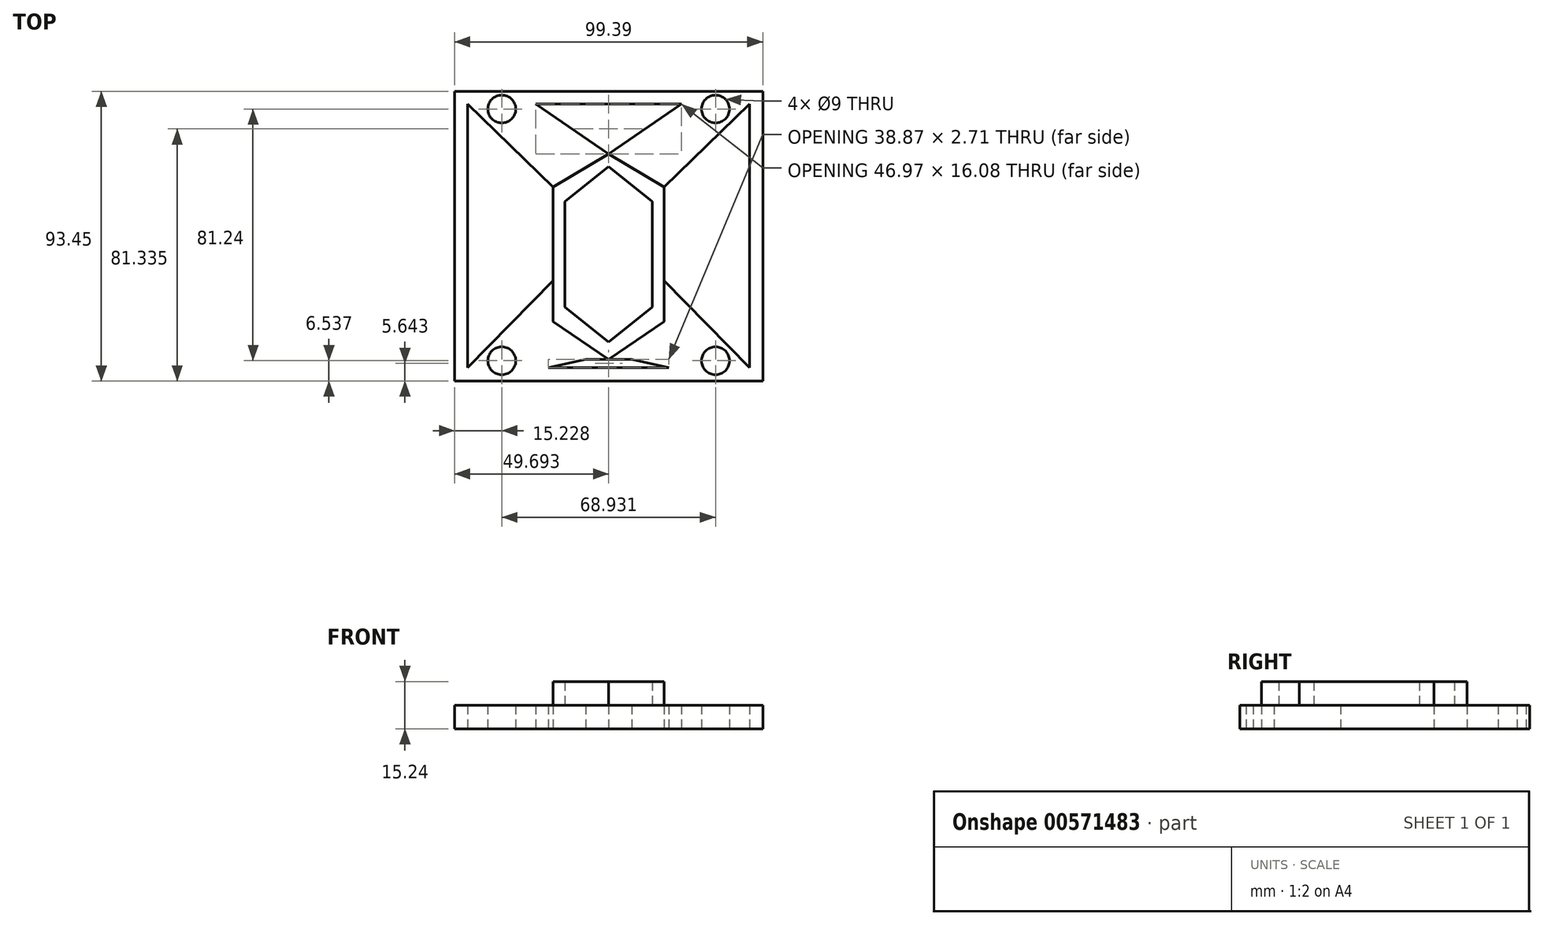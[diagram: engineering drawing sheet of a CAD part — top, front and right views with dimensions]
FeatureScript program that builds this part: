
annotation { "Feature Type Name" : "Feature", "Feature Type Description" : "" }
export const myFeature = defineFeature(function(context is Context, id is Id, definition is map)
    precondition{}
    {
        {
            var Q0;
            Q0=qCreatedBy(makeId("Top.planeOp"),FACE);
            var sketch = newSketch(context, id + "F0", { "sketchPlane" : qUnion([Q0])});
            skLineSegment(sketch, "E0", {"start": v(-15.3, -5.51) * mm, "end": v(-0.48, -5.51) * mm});
            skLineSegment(sketch, "E1", {"start": v(30.61, -12.51) * mm, "end": v(41.8, -12.51) * mm});
            skLineSegment(sketch, "E2.MirrorCS", {"start": v(-46.39, -12.51) * mm, "end": v(-57.58, -12.51) * mm});
            skLineSegment(sketch, "E3", {"start": v(41.8, 80.94) * mm, "end": v(21.56, 80.94) * mm});
            skLineSegment(sketch, "E4.MirrorCS", {"start": v(-57.58, 80.94) * mm, "end": v(-37.33, 80.94) * mm});
            skLineSegment(sketch, "E5", {"start": v(-25.8, 19.92) * mm, "end": v(-25.8, 41.41) * mm});
            skLineSegment(sketch, "E6", {"start": v(10.02, 19.92) * mm, "end": v(10.02, 41.41) * mm});
            skLineSegment(sketch, "E7", {"start": v(-25.8, 41.41) * mm, "end": v(-25.8, 50.1) * mm});
            skLineSegment(sketch, "E8", {"start": v(10.02, 41.41) * mm, "end": v(10.02, 50.1) * mm});
            skLineSegment(sketch, "E9", {"start": v(-37.33, 80.94) * mm, "end": v(21.56, 80.94) * mm});
            skLineSegment(sketch, "E10", {"start": v(15.6, 76.86) * mm, "end": v(-31.37, 76.86) * mm});
            skLineSegment(sketch, "E11", {"start": v(-57.58, 80.94) * mm, "end": v(-57.58, -12.51) * mm});
            skLineSegment(sketch, "E12", {"start": v(-46.39, -12.51) * mm, "end": v(30.61, -12.51) * mm});
            skLineSegment(sketch, "E13", {"start": v(41.8, -12.51) * mm, "end": v(41.8, 80.94) * mm});
            skLineSegment(sketch, "E14", {"start": v(37.6, 76.86) * mm, "end": v(37.6, -8.22) * mm});
            skLineSegment(sketch, "E15", {"start": v(11.55, -8.22) * mm, "end": v(-27.32, -8.22) * mm});
            skLineSegment(sketch, "E16", {"start": v(-53.38, -8.22) * mm, "end": v(-53.38, 76.86) * mm});
            skLineSegment(sketch, "E17", {"start": v(-7.89, 60.79) * mm, "end": v(-7.89, -5.51) * mm, "construction": true});
            skLineSegment(sketch, "E18", {"start": v(-53.38, 76.86) * mm, "end": v(-25.8, 50.1) * mm});
            skLineSegment(sketch, "E19", {"start": v(-31.37, 76.86) * mm, "end": v(-7.89, 60.79) * mm});
            skLineSegment(sketch, "E20", {"start": v(15.6, 76.86) * mm, "end": v(-7.89, 60.79) * mm});
            skLineSegment(sketch, "E21", {"start": v(10.02, 50.1) * mm, "end": v(37.6, 76.86) * mm});
            skLineSegment(sketch, "E22", {"start": v(-25.8, 19.92) * mm, "end": v(-53.38, -8.22) * mm});
            skLineSegment(sketch, "E23", {"start": v(10.02, 19.92) * mm, "end": v(37.6, -8.22) * mm});
            skLineSegment(sketch, "E24", {"start": v(-15.3, -5.51) * mm, "end": v(-27.32, -8.22) * mm});
            skLineSegment(sketch, "E25", {"start": v(-0.48, -5.51) * mm, "end": v(11.55, -8.22) * mm});
            skCircle(sketch, "E26", {"center": v(-42.35, 75.27) * mm, "radius": 4.5 * mm});
            skCircle(sketch, "E27", {"center": v(-42.35, -5.97) * mm, "radius": 4.5 * mm});
            skCircle(sketch, "E28.MirrorC", {"center": v(26.58, 75.27) * mm, "radius": 4.5 * mm});
            skCircle(sketch, "E29.MirrorC", {"center": v(26.58, -5.97) * mm, "radius": 4.5 * mm});
            skSolve(sketch);
        }
        {
            var Q0;
            {var subQ27=sQuery(id+"F0.wireOp",EDGE,"E0");Q0=makeQuery(id+"F0.imprint","IMPRINT",FACE,{"disambiguationData":[TD([[makeQuery(id+"F0.imprint","IMPRINT",EDGE,{"derivedFrom":subQ27}),1.0]])]});}
            var Q1;
            {var subQ0=sQuery(id+"F0.wireOp",EDGE,"E11");Q1=makeQuery(id+"F0.imprint","IMPRINT",FACE,{"disambiguationData":[TD([[makeQuery(id+"F0.imprint","IMPRINT",EDGE,{"derivedFrom":subQ0}),1.0]])]});}
            var Q2;
            {var subQ0=sQuery(id+"F0.wireOp",EDGE,"E13");Q2=makeQuery(id+"F0.imprint","IMPRINT",FACE,{"disambiguationData":[TD([[makeQuery(id+"F0.imprint","IMPRINT",EDGE,{"derivedFrom":subQ0}),1.0]])]});}
            var Q3;
            {var subQ0=sQuery(id+"F0.wireOp",EDGE,"E12");Q3=makeQuery(id+"F0.imprint","IMPRINT",FACE,{"disambiguationData":[TD([[makeQuery(id+"F0.imprint","IMPRINT",EDGE,{"derivedFrom":subQ0}),1.0]])]});}
            var Q4;
            {var subQ0=sQuery(id+"F0.wireOp",EDGE,"E9");Q4=makeQuery(id+"F0.imprint","IMPRINT",FACE,{"disambiguationData":[TD([[makeQuery(id+"F0.imprint","IMPRINT",EDGE,{"derivedFrom":subQ0}),-1.0]])]});}
            extrude(context, id + "F1", {"entities" : qUnion([Q0, Q1, Q2, Q3, Q4]), "depth" : 7.62 * mm, "offsetDistance" : 25.4 * mm});
        }
        {
            var Q0;
            Q0=makeQuery(id+"F1.opExtrude","CAP_FACE",FACE,{"disambiguationData":[OSD([sQuery(id+"F0.wireOp",EDGE,"E0"),sQuery(id+"F0.wireOp",EDGE,"E1"),sQuery(id+"F0.wireOp",EDGE,"E2.MirrorCS"),sQuery(id+"F0.wireOp",EDGE,"WnM6ga3W-2w0Y-njnw-gc1i-JW5yFLPxI45b"),sQuery(id+"F0.wireOp",EDGE,"ALQcIf2C-dGNa-DsCp-nqsF-Dy0OIizcKLJ4"),sQuery(id+"F0.wireOp",EDGE,"E3"),sQuery(id+"F0.wireOp",EDGE,"1HHiR1AF-UmAq-OpZO-W50y-ZvdaEbfYDbQz"),sQuery(id+"F0.wireOp",EDGE,"70f7b64d-7239-4c44-8fee-8d4ab67747ea0.MirrorCS"),sQuery(id+"F0.wireOp",EDGE,"E4.MirrorCS"),sQuery(id+"F0.wireOp",EDGE,"uOv3RaFj-AHeV-BEah-vClL-VHWwjSdkqMHS"),sQuery(id+"F0.wireOp",EDGE,"JlPLlAWy-Zal9-gMeT-OH0J-rQcthV0oo5LD"),sQuery(id+"F0.wireOp",EDGE,"E5"),sQuery(id+"F0.wireOp",EDGE,"E6"),sQuery(id+"F0.wireOp",EDGE,"E7"),sQuery(id+"F0.wireOp",EDGE,"E8"),sQuery(id+"F0.wireOp",EDGE,"sAKVXudm-nMtn-KOFd-aiy5-x48yqmqVD7vz"),sQuery(id+"F0.wireOp",EDGE,"zPrnlccu-b1Of-S2lH-BWAe-agQm7bL7QL2J"),sQuery(id+"F0.wireOp",EDGE,"E9"),sQuery(id+"F0.wireOp",EDGE,"E10"),sQuery(id+"F0.wireOp",EDGE,"E11"),sQuery(id+"F0.wireOp",EDGE,"E12"),sQuery(id+"F0.wireOp",EDGE,"E13"),sQuery(id+"F0.wireOp",EDGE,"E14"),sQuery(id+"F0.wireOp",EDGE,"E15"),sQuery(id+"F0.wireOp",EDGE,"E16")])],"isStart":false});
            var sketch = newSketch(context, id + "F2", { "sketchPlane" : qUnion([Q0])});
            skLineSegment(sketch, "E30", {"start": v(-25.8, 50.1) * mm, "end": v(-7.89, 60.79) * mm});
            skLineSegment(sketch, "E31", {"start": v(10.02, 50.1) * mm, "end": v(-7.89, 60.79) * mm});
            skLineSegment(sketch, "E32", {"start": v(-7.89, 52.55) * mm, "end": v(-7.89, 60.79) * mm});
            skLineSegment(sketch, "E33", {"start": v(-25.8, 19.92) * mm, "end": v(-25.8, 6.62) * mm});
            skLineSegment(sketch, "E34", {"start": v(-25.8, 6.62) * mm, "end": v(-7.89, -5.51) * mm});
            skLineSegment(sketch, "E35", {"start": v(-21.95, 11.35) * mm, "end": v(-7.89, 0) * mm});
            skLineSegment(sketch, "E36.MirrorCS", {"start": v(10.02, 19.92) * mm, "end": v(10.02, 6.62) * mm});
            skLineSegment(sketch, "E37.MirrorCS", {"start": v(10.02, 6.62) * mm, "end": v(-7.89, -5.51) * mm});
            skLineSegment(sketch, "E38.MirrorCS", {"start": v(6.18, 11.35) * mm, "end": v(-7.89, 0) * mm});
            skLineSegment(sketch, "E39", {"start": v(-7.89, 56.67) * mm, "end": v(-21.95, 45.35) * mm});
            skLineSegment(sketch, "E40", {"start": v(-7.89, 56.67) * mm, "end": v(6.18, 45.35) * mm});
            skLineSegment(sketch, "E41", {"start": v(-21.95, 45.35) * mm, "end": v(-21.95, 11.35) * mm});
            skLineSegment(sketch, "E42", {"start": v(6.18, 45.35) * mm, "end": v(6.18, 11.35) * mm});
            skSolve(sketch);
        }
        {
            var Q0;
            Q0=makeQuery(id+"F2.imprint","IMPRINT",FACE,{"disambiguationData":[TD([[makeQuery(id+"F2.imprint","IMPRINT",EDGE,{"derivedFrom":sQuery(id+"F2.wireOp",EDGE,"E30")}),-1.0]])]});
            extrude(context, id + "F3", {"entities" : qUnion([Q0]), "operationType" : NewBodyOperationType.ADD, "depth" : 7.62 * mm, "offsetDistance" : 25.4 * mm});
        }
    });
